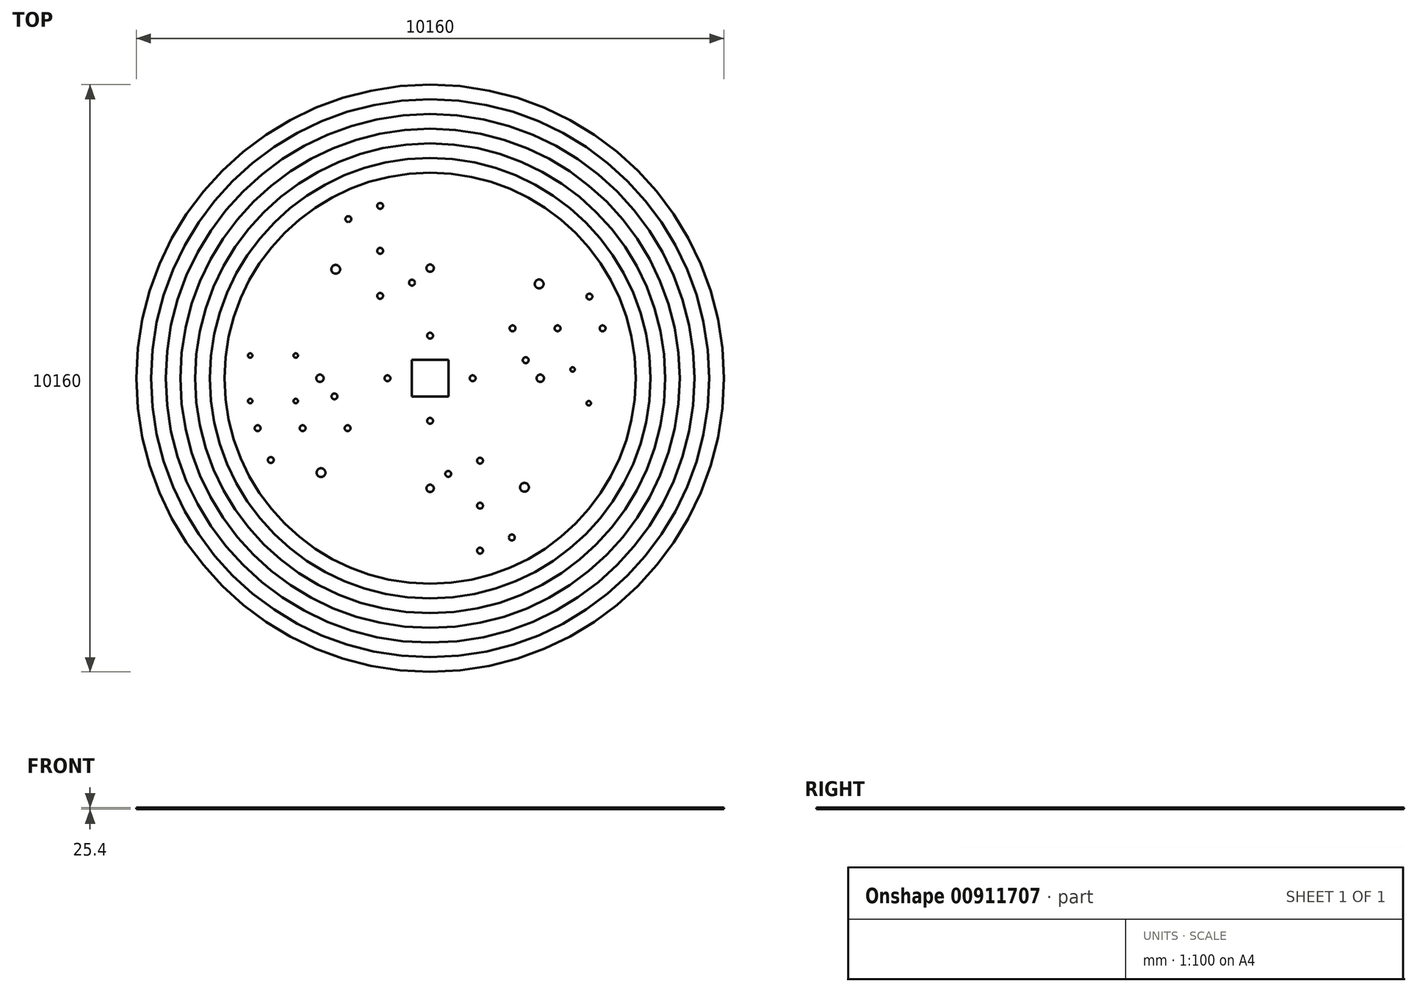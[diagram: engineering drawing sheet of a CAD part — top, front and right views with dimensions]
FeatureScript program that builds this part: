
annotation { "Feature Type Name" : "Feature", "Feature Type Description" : "" }
export const myFeature = defineFeature(function(context is Context, id is Id, definition is map)
    precondition{}
    {
        {
            var Q0;
            Q0=qCreatedBy(makeId("Top.planeOp"),FACE);
            var sketch = newSketch(context, id + "F0", { "sketchPlane" : qUnion([Q0])});
            skCircle(sketch, "E0", {"center": v(0, 736.6) * mm, "radius": 50.8 * mm});
            skLineSegment(sketch, "E1.bottom", {"start": v(-317.5, -317.5) * mm, "end": v(317.5, -317.5) * mm});
            skLineSegment(sketch, "E1.top", {"start": v(-317.5, 317.5) * mm, "end": v(317.5, 317.5) * mm});
            skLineSegment(sketch, "E1.left", {"start": v(-317.5, -317.5) * mm, "end": v(-317.5, 317.5) * mm});
            skLineSegment(sketch, "E1.right", {"start": v(317.5, -317.5) * mm, "end": v(317.5, 317.5) * mm});
            skPoint(sketch, "E1.middle", {"position": v(0, 0) * mm});
            skLineSegment(sketch, "E2", {"start": v(-3111.5, -393.7) * mm, "end": v(-2324.1, -393.7) * mm, "construction": true});
            skPoint(sketch, "E3", {"position": v(-2717.8, -393.7) * mm});
            skCircle(sketch, "E4", {"center": v(-3111.5, -393.7) * mm, "radius": 38.1 * mm});
            skCircle(sketch, "E5", {"center": v(-2324.1, -393.7) * mm, "radius": 38.1 * mm});
            skLineSegment(sketch, "E6", {"start": v(-2717.8, -393.7) * mm, "end": v(-2717.8, 393.7) * mm, "construction": true});
            skLineSegment(sketch, "E7", {"start": v(-3111.5, 393.7) * mm, "end": v(-2324.1, 393.7) * mm, "construction": true});
            skCircle(sketch, "E8", {"center": v(-3111.5, 393.7) * mm, "radius": 38.1 * mm});
            skCircle(sketch, "E9", {"center": v(-2324.1, 393.7) * mm, "radius": 38.1 * mm});
            skCircle(sketch, "E10", {"center": v(0, 0) * mm, "radius": 5080 * mm});
            skCircle(sketch, "E11", {"center": v(-2717.8, 0) * mm, "radius": 38.1 * mm});
            skCircle(sketch, "E12", {"center": v(2743.2, -431.8) * mm, "radius": 38.1 * mm});
            skCircle(sketch, "E13", {"center": v(2463.8, 152.4) * mm, "radius": 38.1 * mm});
            skLineSegment(sketch, "E14.bottom", {"start": v(-635, -635) * mm, "end": v(635, -635) * mm});
            skLineSegment(sketch, "E14.top", {"start": v(-635, 635) * mm, "end": v(635, 635) * mm});
            skLineSegment(sketch, "E14.left", {"start": v(-635, -635) * mm, "end": v(-635, 635) * mm});
            skLineSegment(sketch, "E14.right", {"start": v(635, -635) * mm, "end": v(635, 635) * mm});
            skPoint(sketch, "E15", {"position": v(0, -635) * mm});
            skLineSegment(sketch, "E16.bottom", {"start": v(2463.8, 152.4) * mm, "end": v(2743.2, 152.4) * mm, "construction": true});
            skLineSegment(sketch, "E16.top", {"start": v(2463.8, -431.8) * mm, "end": v(2743.2, -431.8) * mm, "construction": true});
            skLineSegment(sketch, "E16.left", {"start": v(2463.8, 152.4) * mm, "end": v(2463.8, -431.8) * mm, "construction": true});
            skLineSegment(sketch, "E16.right", {"start": v(2743.2, 152.4) * mm, "end": v(2743.2, -431.8) * mm, "construction": true});
            skLineSegment(sketch, "E17.bottom", {"start": v(2400.3, 215.9) * mm, "end": v(2806.7, 215.9) * mm, "construction": true});
            skLineSegment(sketch, "E17.top", {"start": v(2400.3, -495.3) * mm, "end": v(2806.7, -495.3) * mm, "construction": true});
            skLineSegment(sketch, "E17.left", {"start": v(2400.3, 215.9) * mm, "end": v(2400.3, -495.3) * mm, "construction": true});
            skLineSegment(sketch, "E17.right", {"start": v(2806.7, 215.9) * mm, "end": v(2806.7, -495.3) * mm, "construction": true});
            skCircle(sketch, "E18", {"center": v(2743.2, 152.4) * mm, "radius": 38.1 * mm, "construction": true});
            skCircle(sketch, "E19", {"center": v(2463.8, -431.8) * mm, "radius": 38.1 * mm, "construction": true});
            skLineSegment(sketch, "E20", {"start": v(2870.2, -495.3) * mm, "end": v(2870.2, 444.5) * mm});
            skCircle(sketch, "E21", {"center": v(0, 0) * mm, "radius": 2879.57 * mm, "construction": true});
            skLineSegment(sketch, "E22", {"start": v(0, 0) * mm, "end": v(0, -863.6) * mm, "construction": true});
            skLineSegment(sketch, "E23.bottom", {"start": v(-3810, -635) * mm, "end": v(3810, -635) * mm, "construction": true});
            skLineSegment(sketch, "E23.top", {"start": v(-3810, -1176.6) * mm, "end": v(3810, -1176.6) * mm, "construction": true});
            skLineSegment(sketch, "E23.left", {"start": v(-3810, -635) * mm, "end": v(-3810, -1176.6) * mm, "construction": true});
            skLineSegment(sketch, "E23.right", {"start": v(3810, -635) * mm, "end": v(3810, -1176.6) * mm, "construction": true});
            skPoint(sketch, "E24", {"position": v(-635, 635) * mm});
            skLineSegment(sketch, "E25", {"start": v(-3810, -863.6) * mm, "end": v(3810, -863.6) * mm, "construction": true});
            skPoint(sketch, "E26.positionSnap0", {"position": v(0, -863.6) * mm});
            skCircle(sketch, "E27", {"center": v(0, 0) * mm, "radius": 635 * mm, "construction": true});
            skLineSegment(sketch, "E28", {"start": v(0, 0) * mm, "end": v(-2575.42, 2575.42) * mm, "construction": true});
            skPoint(sketch, "E29", {"position": v(-449.01, 449.01) * mm});
            skLineSegment(sketch, "E30", {"start": v(-3143.09, -2245.06) * mm, "end": v(2245.06, 3143.09) * mm, "construction": true});
            skPoint(sketch, "E31", {"position": v(-831.98, 831.98) * mm});
            skPoint(sketch, "E32", {"position": v(-670.34, 670.34) * mm});
            skLineSegment(sketch, "E33", {"start": v(-3364.42, -2023.74) * mm, "end": v(2023.74, 3364.42) * mm, "construction": true});
            skPoint(sketch, "E34", {"position": v(-2204.28, -863.6) * mm});
            skPoint(sketch, "E35", {"position": v(-2074.63, -1176.6) * mm});
            skLineSegment(sketch, "E36", {"start": v(-2204.28, -863.6) * mm, "end": v(-1885.98, -1632.05) * mm});
            skCircle(sketch, "E37", {"center": v(-2204.28, -863.6) * mm, "radius": 50.8 * mm});
            skCircle(sketch, "E38", {"center": v(-2982.5, -863.6) * mm, "radius": 50.8 * mm});
            skCircle(sketch, "E39", {"center": v(-2754.57, -1413.9) * mm, "radius": 50.8 * mm});
            skLineSegment(sketch, "E40", {"start": v(-831.98, 831.98) * mm, "end": v(-3539.53, -1875.56) * mm, "construction": true});
            skCircle(sketch, "E41", {"center": v(-1426.05, -863.6) * mm, "radius": 50.8 * mm});
            skCircle(sketch, "E42", {"center": v(-1653.99, -313.3) * mm, "radius": 50.8 * mm});
            skCircle(sketch, "E43.1.0", {"center": v(-736.6, 0) * mm, "radius": 50.8 * mm});
            skCircle(sketch, "E43.2.0", {"center": v(0, -736.6) * mm, "radius": 50.8 * mm});
            skCircle(sketch, "E43.3.0", {"center": v(736.6, 0) * mm, "radius": 50.8 * mm});
            skCircle(sketch, "E44.1.1", {"center": v(863.6, -1426.05) * mm, "radius": 50.8 * mm});
            skCircle(sketch, "E44.1.2", {"center": v(863.6, -2204.28) * mm, "radius": 50.8 * mm});
            skCircle(sketch, "E44.1.3", {"center": v(313.3, -1653.99) * mm, "radius": 50.8 * mm});
            skCircle(sketch, "E44.1.4", {"center": v(863.6, -2982.5) * mm, "radius": 50.8 * mm});
            skCircle(sketch, "E44.1.5", {"center": v(1413.9, -2754.57) * mm, "radius": 50.8 * mm});
            skCircle(sketch, "E44.2.1", {"center": v(1426.05, 863.6) * mm, "radius": 50.8 * mm});
            skCircle(sketch, "E44.2.2", {"center": v(2204.28, 863.6) * mm, "radius": 50.8 * mm});
            skCircle(sketch, "E44.2.3", {"center": v(1653.99, 313.3) * mm, "radius": 50.8 * mm});
            skCircle(sketch, "E44.2.4", {"center": v(2982.5, 863.6) * mm, "radius": 50.8 * mm});
            skCircle(sketch, "E44.2.5", {"center": v(2754.57, 1413.9) * mm, "radius": 50.8 * mm});
            skCircle(sketch, "E44.3.1", {"center": v(-863.6, 1426.05) * mm, "radius": 50.8 * mm});
            skCircle(sketch, "E44.3.2", {"center": v(-863.6, 2204.28) * mm, "radius": 50.8 * mm});
            skCircle(sketch, "E44.3.3", {"center": v(-313.3, 1653.99) * mm, "radius": 50.8 * mm});
            skCircle(sketch, "E44.3.4", {"center": v(-863.6, 2982.5) * mm, "radius": 50.8 * mm});
            skCircle(sketch, "E44.3.5", {"center": v(-1413.9, 2754.57) * mm, "radius": 50.8 * mm});
            skLineSegment(sketch, "E45", {"start": v(0, 0) * mm, "end": v(-1905, 0) * mm, "construction": true});
            skCircle(sketch, "E46", {"center": v(-1905, 0) * mm, "radius": 63.5 * mm});
            skCircle(sketch, "E47.1.0", {"center": v(0, -1905) * mm, "radius": 63.5 * mm});
            skCircle(sketch, "E47.2.0", {"center": v(1905, 0) * mm, "radius": 63.5 * mm});
            skCircle(sketch, "E48.1.3.0", {"center": v(0, 1905) * mm, "radius": 63.5 * mm});
            skLineSegment(sketch, "E49.bottom", {"start": v(-3302, -3302) * mm, "end": v(3302, -3302) * mm, "construction": true});
            skLineSegment(sketch, "E49.top", {"start": v(-3302, 3302) * mm, "end": v(3302, 3302) * mm, "construction": true});
            skLineSegment(sketch, "E49.left", {"start": v(-3302, -3302) * mm, "end": v(-3302, 3302) * mm, "construction": true});
            skLineSegment(sketch, "E49.right", {"start": v(3302, -3302) * mm, "end": v(3302, 3302) * mm, "construction": true});
            skLineSegment(sketch, "E50.bottom", {"start": v(-2908.3, -190.5) * mm, "end": v(-2527.3, -190.5) * mm, "construction": true});
            skLineSegment(sketch, "E50.top", {"start": v(-2908.3, 190.5) * mm, "end": v(-2527.3, 190.5) * mm, "construction": true});
            skLineSegment(sketch, "E50.left", {"start": v(-2908.3, -190.5) * mm, "end": v(-2908.3, 190.5) * mm, "construction": true});
            skLineSegment(sketch, "E50.right", {"start": v(-2527.3, -190.5) * mm, "end": v(-2527.3, 190.5) * mm, "construction": true});
            skCircle(sketch, "E51", {"center": v(-2908.3, 190.5) * mm, "radius": 50.8 * mm});
            skCircle(sketch, "E52", {"center": v(-2527.3, 190.5) * mm, "radius": 50.8 * mm});
            skCircle(sketch, "E53", {"center": v(-2908.3, -190.5) * mm, "radius": 50.8 * mm});
            skCircle(sketch, "E54", {"center": v(-2527.3, -190.5) * mm, "radius": 50.8 * mm});
            skCircle(sketch, "E55", {"center": v(-1885.98, -1632.05) * mm, "radius": 455.44 * mm, "construction": true});
            skCircle(sketch, "E56", {"center": v(-1885.98, -1632.05) * mm, "radius": 76.2 * mm});
            skCircle(sketch, "E57.1.0", {"center": v(1632.05, -1885.98) * mm, "radius": 76.2 * mm});
            skCircle(sketch, "E57.2.0", {"center": v(1885.98, 1632.05) * mm, "radius": 76.2 * mm});
            skCircle(sketch, "E57.3.0", {"center": v(-1632.05, 1885.98) * mm, "radius": 76.2 * mm});
            skLineSegment(sketch, "E58", {"start": v(0, 0) * mm, "end": v(-3683, 0) * mm, "construction": true});
            skCircle(sketch, "E59", {"center": v(0, 0) * mm, "radius": 4826 * mm});
            skCircle(sketch, "E60", {"center": v(0, 0) * mm, "radius": 4572 * mm});
            skCircle(sketch, "E61", {"center": v(0, 0) * mm, "radius": 4318 * mm});
            skCircle(sketch, "E62", {"center": v(0, 0) * mm, "radius": 3810 * mm});
            skCircle(sketch, "E63", {"center": v(0, 0) * mm, "radius": 4064 * mm});
            skCircle(sketch, "E64", {"center": v(0, 0) * mm, "radius": 3556 * mm});
            skSolve(sketch);
        }
        {
            var Q0;
            Q0=makeQuery(id+"F0.imprint","IMPRINT",FACE,{"disambiguationData":[TD([[makeQuery(id+"F0.imprint","IMPRINT",EDGE,{"derivedFrom":sQuery(id+"F0.wireOp",EDGE,"E0")}),-1.0]])]});
            var Q1;
            Q1=makeQuery(id+"F0.imprint","IMPRINT",FACE,{"disambiguationData":[TD([[makeQuery(id+"F0.imprint","IMPRINT",EDGE,{"derivedFrom":sQuery(id+"F0.wireOp",EDGE,"E1.bottom")}),-1.0]])]});
            var Q2;
            Q2=makeQuery(id+"F0.imprint","IMPRINT",FACE,{"disambiguationData":[TD([[makeQuery(id+"F0.imprint","IMPRINT",EDGE,{"derivedFrom":sQuery(id+"F0.wireOp",EDGE,"E52")}),1.0]])]});
            var Q3;
            Q3=makeQuery(id+"F0.imprint","IMPRINT",FACE,{"disambiguationData":[TD([[makeQuery(id+"F0.imprint","IMPRINT",EDGE,{"derivedFrom":sQuery(id+"F0.wireOp",EDGE,"E54")}),1.0]])]});
            var Q4;
            Q4=makeQuery(id+"F0.imprint","IMPRINT",FACE,{"disambiguationData":[TD([[makeQuery(id+"F0.imprint","IMPRINT",EDGE,{"derivedFrom":sQuery(id+"F0.wireOp",EDGE,"E51")}),1.0]])]});
            var Q5;
            Q5=makeQuery(id+"F0.imprint","IMPRINT",FACE,{"disambiguationData":[TD([[makeQuery(id+"F0.imprint","IMPRINT",EDGE,{"derivedFrom":sQuery(id+"F0.wireOp",EDGE,"E11")}),1.0]])]});
            var Q6;
            Q6=makeQuery(id+"F0.imprint","IMPRINT",FACE,{"disambiguationData":[TD([[makeQuery(id+"F0.imprint","IMPRINT",EDGE,{"derivedFrom":sQuery(id+"F0.wireOp",EDGE,"E53")}),1.0]])]});
            extrude(context, id + "F1", {"entities" : qUnion([Q0, Q1, Q2, Q3, Q4, Q5, Q6]), "depth" : 25.4 * mm, "offsetDistance" : 25.4 * mm});
        }
        {
            var Q0;
            Q0=makeQuery(id+"F0.imprint","IMPRINT",FACE,{"disambiguationData":[TD([[makeQuery(id+"F0.imprint","IMPRINT",EDGE,{"derivedFrom":sQuery(id+"F0.wireOp",EDGE,"E0")}),-1.0]])]});
            var Q1;
            Q1=makeQuery(id+"F0.imprint","IMPRINT",FACE,{"disambiguationData":[TD([[makeQuery(id+"F0.imprint","IMPRINT",EDGE,{"derivedFrom":sQuery(id+"F0.wireOp",EDGE,"E62")}),1.0]])]});
            var Q2;
            Q2=makeQuery(id+"F0.imprint","IMPRINT",FACE,{"disambiguationData":[TD([[makeQuery(id+"F0.imprint","IMPRINT",EDGE,{"derivedFrom":sQuery(id+"F0.wireOp",EDGE,"E53")}),1.0]])]});
            var Q3;
            Q3=makeQuery(id+"F0.imprint","IMPRINT",FACE,{"disambiguationData":[TD([[makeQuery(id+"F0.imprint","IMPRINT",EDGE,{"derivedFrom":sQuery(id+"F0.wireOp",EDGE,"E51")}),1.0]])]});
            var Q4;
            Q4=makeQuery(id+"F0.imprint","IMPRINT",FACE,{"disambiguationData":[TD([[makeQuery(id+"F0.imprint","IMPRINT",EDGE,{"derivedFrom":sQuery(id+"F0.wireOp",EDGE,"E52")}),1.0]])]});
            var Q5;
            Q5=makeQuery(id+"F0.imprint","IMPRINT",FACE,{"disambiguationData":[TD([[makeQuery(id+"F0.imprint","IMPRINT",EDGE,{"derivedFrom":sQuery(id+"F0.wireOp",EDGE,"E54")}),1.0]])]});
            var Q6;
            Q6=makeQuery(id+"F0.imprint","IMPRINT",FACE,{"disambiguationData":[TD([[makeQuery(id+"F0.imprint","IMPRINT",EDGE,{"derivedFrom":sQuery(id+"F0.wireOp",EDGE,"E11")}),1.0]])]});
            var Q7;
            Q7=makeQuery(id+"F0.imprint","IMPRINT",FACE,{"disambiguationData":[TD([[makeQuery(id+"F0.imprint","IMPRINT",EDGE,{"derivedFrom":sQuery(id+"F0.wireOp",EDGE,"E1.bottom")}),-1.0]])]});
            extrude(context, id + "F2", {"entities" : qUnion([Q0, Q1, Q2, Q3, Q4, Q5, Q6, Q7]), "depth" : 25.4 * mm, "offsetDistance" : 25.4 * mm});
        }
        {
            var Q0;
            Q0=makeQuery(id+"F0.imprint","IMPRINT",FACE,{"disambiguationData":[TD([[makeQuery(id+"F0.imprint","IMPRINT",EDGE,{"derivedFrom":sQuery(id+"F0.wireOp",EDGE,"E62")}),-1.0]])]});
            var Q1;
            Q1=makeQuery(id+"F0.imprint","IMPRINT",FACE,{"disambiguationData":[TD([[makeQuery(id+"F0.imprint","IMPRINT",EDGE,{"derivedFrom":sQuery(id+"F0.wireOp",EDGE,"E62")}),1.0]])]});
            var Q2;
            Q2=makeQuery(id+"F0.imprint","IMPRINT",FACE,{"disambiguationData":[TD([[makeQuery(id+"F0.imprint","IMPRINT",EDGE,{"derivedFrom":sQuery(id+"F0.wireOp",EDGE,"E0")}),-1.0]])]});
            var Q3;
            Q3=makeQuery(id+"F0.imprint","IMPRINT",FACE,{"disambiguationData":[TD([[makeQuery(id+"F0.imprint","IMPRINT",EDGE,{"derivedFrom":sQuery(id+"F0.wireOp",EDGE,"E1.bottom")}),-1.0]])]});
            var Q4;
            Q4=makeQuery(id+"F0.imprint","IMPRINT",FACE,{"disambiguationData":[TD([[makeQuery(id+"F0.imprint","IMPRINT",EDGE,{"derivedFrom":sQuery(id+"F0.wireOp",EDGE,"E51")}),1.0]])]});
            var Q5;
            Q5=makeQuery(id+"F0.imprint","IMPRINT",FACE,{"disambiguationData":[TD([[makeQuery(id+"F0.imprint","IMPRINT",EDGE,{"derivedFrom":sQuery(id+"F0.wireOp",EDGE,"E52")}),1.0]])]});
            var Q6;
            Q6=makeQuery(id+"F0.imprint","IMPRINT",FACE,{"disambiguationData":[TD([[makeQuery(id+"F0.imprint","IMPRINT",EDGE,{"derivedFrom":sQuery(id+"F0.wireOp",EDGE,"E54")}),1.0]])]});
            var Q7;
            Q7=makeQuery(id+"F0.imprint","IMPRINT",FACE,{"disambiguationData":[TD([[makeQuery(id+"F0.imprint","IMPRINT",EDGE,{"derivedFrom":sQuery(id+"F0.wireOp",EDGE,"E11")}),1.0]])]});
            var Q8;
            Q8=makeQuery(id+"F0.imprint","IMPRINT",FACE,{"disambiguationData":[TD([[makeQuery(id+"F0.imprint","IMPRINT",EDGE,{"derivedFrom":sQuery(id+"F0.wireOp",EDGE,"E53")}),1.0]])]});
            extrude(context, id + "F3", {"entities" : qUnion([Q0, Q1, Q2, Q3, Q4, Q5, Q6, Q7, Q8]), "depth" : 25.4 * mm, "offsetDistance" : 25.4 * mm});
        }
        {
            var Q0;
            Q0=makeQuery(id+"F0.imprint","IMPRINT",FACE,{"disambiguationData":[TD([[makeQuery(id+"F0.imprint","IMPRINT",EDGE,{"derivedFrom":sQuery(id+"F0.wireOp",EDGE,"E61")}),1.0]])]});
            var Q1;
            Q1=makeQuery(id+"F0.imprint","IMPRINT",FACE,{"disambiguationData":[TD([[makeQuery(id+"F0.imprint","IMPRINT",EDGE,{"derivedFrom":sQuery(id+"F0.wireOp",EDGE,"E62")}),-1.0]])]});
            var Q2;
            Q2=makeQuery(id+"F0.imprint","IMPRINT",FACE,{"disambiguationData":[TD([[makeQuery(id+"F0.imprint","IMPRINT",EDGE,{"derivedFrom":sQuery(id+"F0.wireOp",EDGE,"E62")}),1.0]])]});
            var Q3;
            Q3=makeQuery(id+"F0.imprint","IMPRINT",FACE,{"disambiguationData":[TD([[makeQuery(id+"F0.imprint","IMPRINT",EDGE,{"derivedFrom":sQuery(id+"F0.wireOp",EDGE,"E0")}),-1.0]])]});
            var Q4;
            Q4=makeQuery(id+"F0.imprint","IMPRINT",FACE,{"disambiguationData":[TD([[makeQuery(id+"F0.imprint","IMPRINT",EDGE,{"derivedFrom":sQuery(id+"F0.wireOp",EDGE,"E1.bottom")}),-1.0]])]});
            var Q5;
            Q5=makeQuery(id+"F0.imprint","IMPRINT",FACE,{"disambiguationData":[TD([[makeQuery(id+"F0.imprint","IMPRINT",EDGE,{"derivedFrom":sQuery(id+"F0.wireOp",EDGE,"E51")}),1.0]])]});
            var Q6;
            Q6=makeQuery(id+"F0.imprint","IMPRINT",FACE,{"disambiguationData":[TD([[makeQuery(id+"F0.imprint","IMPRINT",EDGE,{"derivedFrom":sQuery(id+"F0.wireOp",EDGE,"E52")}),1.0]])]});
            var Q7;
            Q7=makeQuery(id+"F0.imprint","IMPRINT",FACE,{"disambiguationData":[TD([[makeQuery(id+"F0.imprint","IMPRINT",EDGE,{"derivedFrom":sQuery(id+"F0.wireOp",EDGE,"E54")}),1.0]])]});
            var Q8;
            Q8=makeQuery(id+"F0.imprint","IMPRINT",FACE,{"disambiguationData":[TD([[makeQuery(id+"F0.imprint","IMPRINT",EDGE,{"derivedFrom":sQuery(id+"F0.wireOp",EDGE,"E11")}),1.0]])]});
            var Q9;
            Q9=makeQuery(id+"F0.imprint","IMPRINT",FACE,{"disambiguationData":[TD([[makeQuery(id+"F0.imprint","IMPRINT",EDGE,{"derivedFrom":sQuery(id+"F0.wireOp",EDGE,"E53")}),1.0]])]});
            extrude(context, id + "F4", {"entities" : qUnion([Q0, Q1, Q2, Q3, Q4, Q5, Q6, Q7, Q8, Q9]), "depth" : 25.4 * mm, "offsetDistance" : 25.4 * mm});
        }
        {
            var Q0;
            Q0=makeQuery(id+"F0.imprint","IMPRINT",FACE,{"disambiguationData":[TD([[makeQuery(id+"F0.imprint","IMPRINT",EDGE,{"derivedFrom":sQuery(id+"F0.wireOp",EDGE,"E60")}),1.0]])]});
            var Q1;
            Q1=makeQuery(id+"F0.imprint","IMPRINT",FACE,{"disambiguationData":[TD([[makeQuery(id+"F0.imprint","IMPRINT",EDGE,{"derivedFrom":sQuery(id+"F0.wireOp",EDGE,"E61")}),1.0]])]});
            var Q2;
            Q2=makeQuery(id+"F0.imprint","IMPRINT",FACE,{"disambiguationData":[TD([[makeQuery(id+"F0.imprint","IMPRINT",EDGE,{"derivedFrom":sQuery(id+"F0.wireOp",EDGE,"E62")}),-1.0]])]});
            var Q3;
            Q3=makeQuery(id+"F0.imprint","IMPRINT",FACE,{"disambiguationData":[TD([[makeQuery(id+"F0.imprint","IMPRINT",EDGE,{"derivedFrom":sQuery(id+"F0.wireOp",EDGE,"E62")}),1.0]])]});
            var Q4;
            Q4=makeQuery(id+"F0.imprint","IMPRINT",FACE,{"disambiguationData":[TD([[makeQuery(id+"F0.imprint","IMPRINT",EDGE,{"derivedFrom":sQuery(id+"F0.wireOp",EDGE,"E1.bottom")}),-1.0]])]});
            var Q5;
            Q5=makeQuery(id+"F0.imprint","IMPRINT",FACE,{"disambiguationData":[TD([[makeQuery(id+"F0.imprint","IMPRINT",EDGE,{"derivedFrom":sQuery(id+"F0.wireOp",EDGE,"E0")}),-1.0]])]});
            var Q6;
            Q6=makeQuery(id+"F0.imprint","IMPRINT",FACE,{"disambiguationData":[TD([[makeQuery(id+"F0.imprint","IMPRINT",EDGE,{"derivedFrom":sQuery(id+"F0.wireOp",EDGE,"E51")}),1.0]])]});
            var Q7;
            Q7=makeQuery(id+"F0.imprint","IMPRINT",FACE,{"disambiguationData":[TD([[makeQuery(id+"F0.imprint","IMPRINT",EDGE,{"derivedFrom":sQuery(id+"F0.wireOp",EDGE,"E52")}),1.0]])]});
            var Q8;
            Q8=makeQuery(id+"F0.imprint","IMPRINT",FACE,{"disambiguationData":[TD([[makeQuery(id+"F0.imprint","IMPRINT",EDGE,{"derivedFrom":sQuery(id+"F0.wireOp",EDGE,"E54")}),1.0]])]});
            var Q9;
            Q9=makeQuery(id+"F0.imprint","IMPRINT",FACE,{"disambiguationData":[TD([[makeQuery(id+"F0.imprint","IMPRINT",EDGE,{"derivedFrom":sQuery(id+"F0.wireOp",EDGE,"E53")}),1.0]])]});
            var Q10;
            Q10=makeQuery(id+"F0.imprint","IMPRINT",FACE,{"disambiguationData":[TD([[makeQuery(id+"F0.imprint","IMPRINT",EDGE,{"derivedFrom":sQuery(id+"F0.wireOp",EDGE,"E11")}),1.0]])]});
            extrude(context, id + "F5", {"entities" : qUnion([Q0, Q1, Q2, Q3, Q4, Q5, Q6, Q7, Q8, Q9, Q10]), "depth" : 25.4 * mm, "offsetDistance" : 25.4 * mm});
        }
        {
            var Q0;
            Q0=makeQuery(id+"F0.imprint","IMPRINT",FACE,{"disambiguationData":[TD([[makeQuery(id+"F0.imprint","IMPRINT",EDGE,{"derivedFrom":sQuery(id+"F0.wireOp",EDGE,"E59")}),1.0]])]});
            var Q1;
            Q1=makeQuery(id+"F0.imprint","IMPRINT",FACE,{"disambiguationData":[TD([[makeQuery(id+"F0.imprint","IMPRINT",EDGE,{"derivedFrom":sQuery(id+"F0.wireOp",EDGE,"E60")}),1.0]])]});
            var Q2;
            Q2=makeQuery(id+"F0.imprint","IMPRINT",FACE,{"disambiguationData":[TD([[makeQuery(id+"F0.imprint","IMPRINT",EDGE,{"derivedFrom":sQuery(id+"F0.wireOp",EDGE,"E61")}),1.0]])]});
            var Q3;
            Q3=makeQuery(id+"F0.imprint","IMPRINT",FACE,{"disambiguationData":[TD([[makeQuery(id+"F0.imprint","IMPRINT",EDGE,{"derivedFrom":sQuery(id+"F0.wireOp",EDGE,"E62")}),-1.0]])]});
            var Q4;
            Q4=makeQuery(id+"F0.imprint","IMPRINT",FACE,{"disambiguationData":[TD([[makeQuery(id+"F0.imprint","IMPRINT",EDGE,{"derivedFrom":sQuery(id+"F0.wireOp",EDGE,"E62")}),1.0]])]});
            var Q5;
            Q5=makeQuery(id+"F0.imprint","IMPRINT",FACE,{"disambiguationData":[TD([[makeQuery(id+"F0.imprint","IMPRINT",EDGE,{"derivedFrom":sQuery(id+"F0.wireOp",EDGE,"E0")}),-1.0]])]});
            var Q6;
            Q6=makeQuery(id+"F0.imprint","IMPRINT",FACE,{"disambiguationData":[TD([[makeQuery(id+"F0.imprint","IMPRINT",EDGE,{"derivedFrom":sQuery(id+"F0.wireOp",EDGE,"E1.bottom")}),-1.0]])]});
            var Q7;
            Q7=makeQuery(id+"F0.imprint","IMPRINT",FACE,{"disambiguationData":[TD([[makeQuery(id+"F0.imprint","IMPRINT",EDGE,{"derivedFrom":sQuery(id+"F0.wireOp",EDGE,"E51")}),1.0]])]});
            var Q8;
            Q8=makeQuery(id+"F0.imprint","IMPRINT",FACE,{"disambiguationData":[TD([[makeQuery(id+"F0.imprint","IMPRINT",EDGE,{"derivedFrom":sQuery(id+"F0.wireOp",EDGE,"E52")}),1.0]])]});
            var Q9;
            Q9=makeQuery(id+"F0.imprint","IMPRINT",FACE,{"disambiguationData":[TD([[makeQuery(id+"F0.imprint","IMPRINT",EDGE,{"derivedFrom":sQuery(id+"F0.wireOp",EDGE,"E11")}),1.0]])]});
            var Q10;
            Q10=makeQuery(id+"F0.imprint","IMPRINT",FACE,{"disambiguationData":[TD([[makeQuery(id+"F0.imprint","IMPRINT",EDGE,{"derivedFrom":sQuery(id+"F0.wireOp",EDGE,"E53")}),1.0]])]});
            var Q11;
            Q11=makeQuery(id+"F0.imprint","IMPRINT",FACE,{"disambiguationData":[TD([[makeQuery(id+"F0.imprint","IMPRINT",EDGE,{"derivedFrom":sQuery(id+"F0.wireOp",EDGE,"E54")}),1.0]])]});
            extrude(context, id + "F6", {"entities" : qUnion([Q0, Q1, Q2, Q3, Q4, Q5, Q6, Q7, Q8, Q9, Q10, Q11]), "depth" : 25.4 * mm, "offsetDistance" : 25.4 * mm});
        }
        {
            var Q0;
            Q0=makeQuery(id+"F0.imprint","IMPRINT",FACE,{"disambiguationData":[TD([[makeQuery(id+"F0.imprint","IMPRINT",EDGE,{"derivedFrom":sQuery(id+"F0.wireOp",EDGE,"E10")}),1.0]])]});
            var Q1;
            Q1=makeQuery(id+"F0.imprint","IMPRINT",FACE,{"disambiguationData":[TD([[makeQuery(id+"F0.imprint","IMPRINT",EDGE,{"derivedFrom":sQuery(id+"F0.wireOp",EDGE,"E59")}),1.0]])]});
            var Q2;
            Q2=makeQuery(id+"F0.imprint","IMPRINT",FACE,{"disambiguationData":[TD([[makeQuery(id+"F0.imprint","IMPRINT",EDGE,{"derivedFrom":sQuery(id+"F0.wireOp",EDGE,"E60")}),1.0]])]});
            var Q3;
            Q3=makeQuery(id+"F0.imprint","IMPRINT",FACE,{"disambiguationData":[TD([[makeQuery(id+"F0.imprint","IMPRINT",EDGE,{"derivedFrom":sQuery(id+"F0.wireOp",EDGE,"E61")}),1.0]])]});
            var Q4;
            Q4=makeQuery(id+"F0.imprint","IMPRINT",FACE,{"disambiguationData":[TD([[makeQuery(id+"F0.imprint","IMPRINT",EDGE,{"derivedFrom":sQuery(id+"F0.wireOp",EDGE,"E62")}),-1.0]])]});
            var Q5;
            Q5=makeQuery(id+"F0.imprint","IMPRINT",FACE,{"disambiguationData":[TD([[makeQuery(id+"F0.imprint","IMPRINT",EDGE,{"derivedFrom":sQuery(id+"F0.wireOp",EDGE,"E62")}),1.0]])]});
            var Q6;
            Q6=makeQuery(id+"F0.imprint","IMPRINT",FACE,{"disambiguationData":[TD([[makeQuery(id+"F0.imprint","IMPRINT",EDGE,{"derivedFrom":sQuery(id+"F0.wireOp",EDGE,"E0")}),-1.0]])]});
            var Q7;
            Q7=makeQuery(id+"F0.imprint","IMPRINT",FACE,{"disambiguationData":[TD([[makeQuery(id+"F0.imprint","IMPRINT",EDGE,{"derivedFrom":sQuery(id+"F0.wireOp",EDGE,"E1.bottom")}),-1.0]])]});
            var Q8;
            Q8=makeQuery(id+"F0.imprint","IMPRINT",FACE,{"disambiguationData":[TD([[makeQuery(id+"F0.imprint","IMPRINT",EDGE,{"derivedFrom":sQuery(id+"F0.wireOp",EDGE,"E51")}),1.0]])]});
            var Q9;
            Q9=makeQuery(id+"F0.imprint","IMPRINT",FACE,{"disambiguationData":[TD([[makeQuery(id+"F0.imprint","IMPRINT",EDGE,{"derivedFrom":sQuery(id+"F0.wireOp",EDGE,"E52")}),1.0]])]});
            var Q10;
            Q10=makeQuery(id+"F0.imprint","IMPRINT",FACE,{"disambiguationData":[TD([[makeQuery(id+"F0.imprint","IMPRINT",EDGE,{"derivedFrom":sQuery(id+"F0.wireOp",EDGE,"E54")}),1.0]])]});
            var Q11;
            Q11=makeQuery(id+"F0.imprint","IMPRINT",FACE,{"disambiguationData":[TD([[makeQuery(id+"F0.imprint","IMPRINT",EDGE,{"derivedFrom":sQuery(id+"F0.wireOp",EDGE,"E11")}),1.0]])]});
            var Q12;
            Q12=makeQuery(id+"F0.imprint","IMPRINT",FACE,{"disambiguationData":[TD([[makeQuery(id+"F0.imprint","IMPRINT",EDGE,{"derivedFrom":sQuery(id+"F0.wireOp",EDGE,"E53")}),1.0]])]});
            extrude(context, id + "F7", {"entities" : qUnion([Q0, Q1, Q2, Q3, Q4, Q5, Q6, Q7, Q8, Q9, Q10, Q11, Q12]), "depth" : 25.4 * mm, "offsetDistance" : 25.4 * mm});
        }
    });
